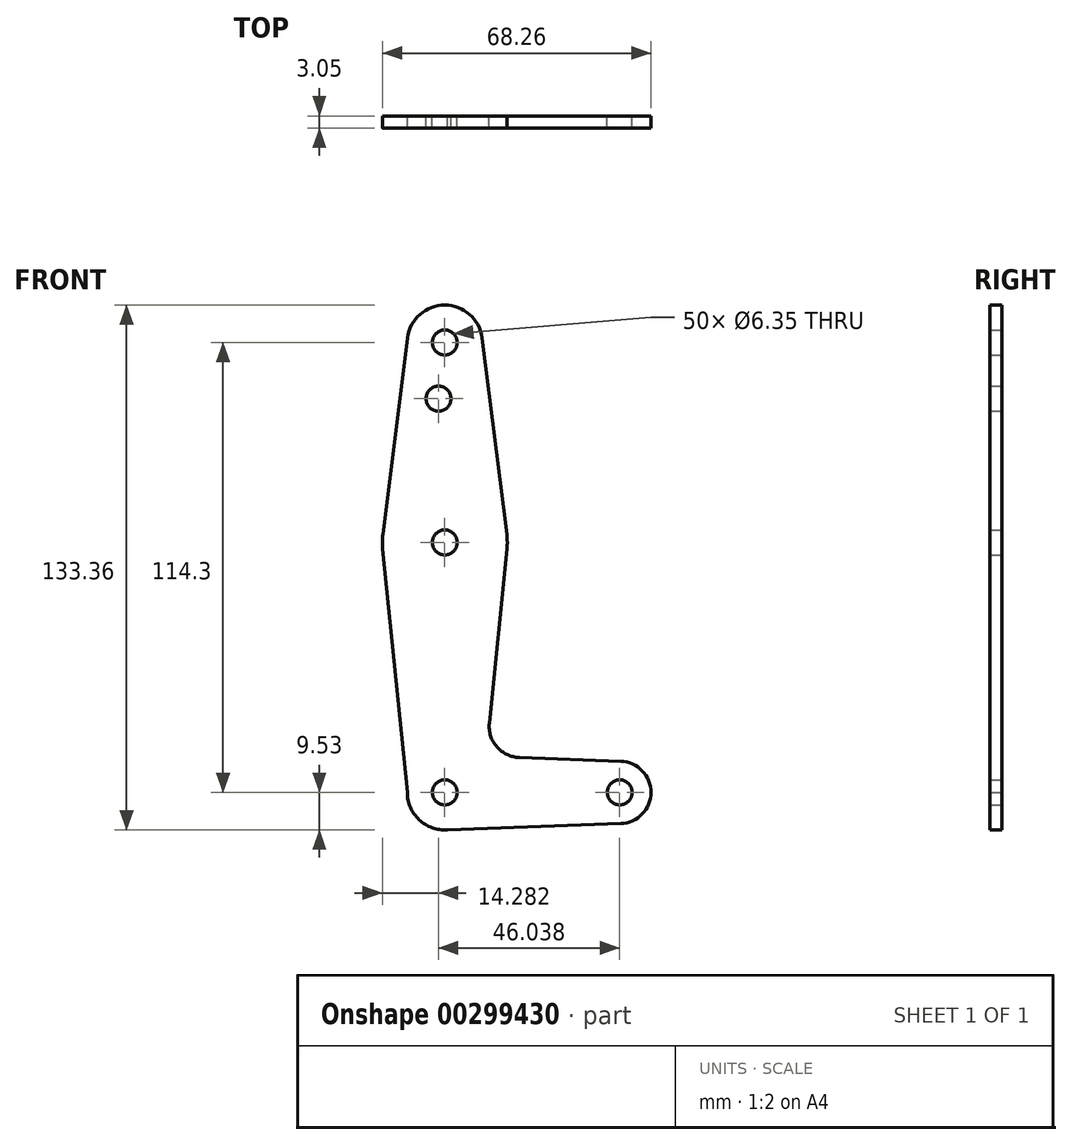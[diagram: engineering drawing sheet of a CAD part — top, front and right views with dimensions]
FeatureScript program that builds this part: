
annotation { "Feature Type Name" : "Feature", "Feature Type Description" : "" }
export const myFeature = defineFeature(function(context is Context, id is Id, definition is map)
    precondition{}
    {
        {
            var Q0;
            Q0=qCreatedBy(makeId("Front.planeOp"),FACE);
            var sketch = newSketch(context, id + "F0", { "sketchPlane" : qUnion([Q0])});
            skCircle(sketch, "E0", {"center": v(0, 0) * mm, "radius": 9.53 * mm});
            skCircle(sketch, "E1", {"center": v(0, 63.5) * mm, "radius": 15.88 * mm});
            skCircle(sketch, "E2", {"center": v(0, 114.3) * mm, "radius": 9.53 * mm});
            skCircle(sketch, "E3", {"center": v(44.45, 0) * mm, "radius": 7.94 * mm});
            skLineSegment(sketch, "E4", {"start": v(0, 114.3) * mm, "end": v(0, 63.5) * mm, "construction": true});
            skLineSegment(sketch, "E5", {"start": v(0, 63.5) * mm, "end": v(0, 0) * mm, "construction": true});
            skLineSegment(sketch, "E6", {"start": v(0, 0) * mm, "end": v(44.45, 0) * mm, "construction": true});
            skLineSegment(sketch, "E7", {"start": v(-9.45, 115.5) * mm, "end": v(-15.75, 65.48) * mm});
            skLineSegment(sketch, "E8", {"start": v(-9.53, 0) * mm, "end": v(-15.8, 61.9) * mm});
            skLineSegment(sketch, "E9", {"start": v(9.45, 115.5) * mm, "end": v(15.75, 65.48) * mm});
            skLineSegment(sketch, "E10", {"start": v(11.3, 17.6) * mm, "end": v(15.8, 61.9) * mm});
            skLineSegment(sketch, "E11", {"start": v(0, -9.53) * mm, "end": v(44.73, -7.93) * mm});
            skLineSegment(sketch, "E12", {"start": v(18.93, 8.85) * mm, "end": v(44.73, 7.93) * mm});
            skCircle(sketch, "E13", {"center": v(0, 114.3) * mm, "radius": 3.18 * mm});
            skCircle(sketch, "E14", {"center": v(0, 63.5) * mm, "radius": 3.18 * mm});
            skCircle(sketch, "E15", {"center": v(0, 0) * mm, "radius": 3.18 * mm});
            skCircle(sketch, "E16", {"center": v(44.45, 0) * mm, "radius": 3.18 * mm});
            skCircle(sketch, "E17", {"center": v(-1.59, 100.03) * mm, "radius": 3.18 * mm});
            skArc(sketch, "E18.filletArc", {"start": v(11.3, 17.6) * mm, "mid": v(13.22, 11.57) * mm, "end": v(18.93, 8.85) * mm});
            skSolve(sketch);
        }
        {
            var Q0;
            Q0 = qSketchRegion(id + "F0", true);
            extrude(context, id + "F1", {"entities" : qUnion([Q0]), "depth" : 3.05 * mm});
        }
    });
